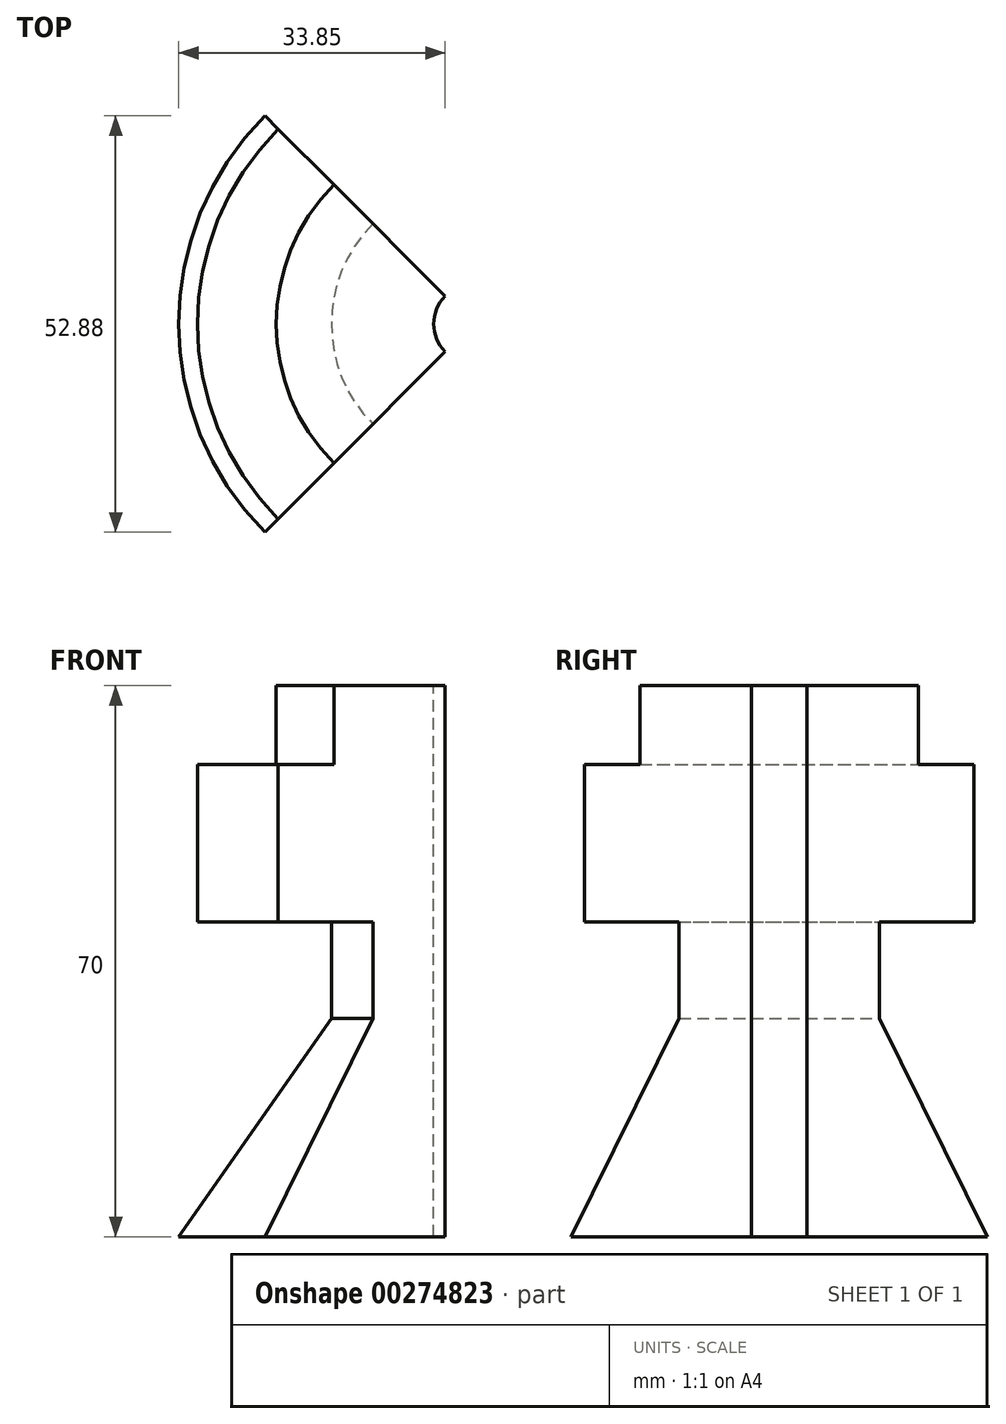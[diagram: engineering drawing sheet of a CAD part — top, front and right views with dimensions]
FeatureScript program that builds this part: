
annotation { "Feature Type Name" : "Feature", "Feature Type Description" : "" }
export const myFeature = defineFeature(function(context is Context, id is Id, definition is map)
    precondition{}
    {
        {
            var Q0;
            Q0=qCreatedBy(makeId("Front.planeOp"),FACE);
            var sketch = newSketch(context, id + "F0", { "sketchPlane" : qUnion([Q0])});
            skLineSegment(sketch, "E0", {"start": v(0, 0) * mm, "end": v(0, 40) * mm});
            skLineSegment(sketch, "E1", {"start": v(0, 40) * mm, "end": v(-25, 40) * mm});
            skLineSegment(sketch, "E2", {"start": v(-25, 40) * mm, "end": v(-25, 30) * mm});
            skLineSegment(sketch, "E3", {"start": v(-25, 30) * mm, "end": v(-35, 30) * mm});
            skLineSegment(sketch, "E4", {"start": v(-35, 30) * mm, "end": v(-35, 10) * mm});
            skLineSegment(sketch, "E5", {"start": v(-35, 10) * mm, "end": v(-18, 10) * mm});
            skLineSegment(sketch, "E6", {"start": v(-18, 10) * mm, "end": v(-18, -2.3) * mm});
            skLineSegment(sketch, "E7", {"start": v(-18, -2.3) * mm, "end": v(-37.4, -30) * mm});
            skLineSegment(sketch, "E8", {"start": v(-37.4, -30) * mm, "end": v(0, -30) * mm});
            skLineSegment(sketch, "E9", {"start": v(0, -30) * mm, "end": v(0, 0) * mm});
            skSolve(sketch);
        }
        {
            var Q0;
            Q0 = qSketchRegion(id + "F0", true);
            var Q1;
            Q1=sQuery(id+"F0.wireOp",EDGE,"E0");
            revolve(context, id + "F1", {"entities" : qUnion([Q0]), "axis" : qUnion([Q1]), "revolveType" : RevolveType.SYMMETRIC, "angle" : 90 * degree});
        }
        {
            var Q0;
            Q0=makeQuery(id+"F1.opRevolve","SWEPT_FACE",FACE,{"disambiguationData":[OSD([sQuery(id+"F0.wireOp",EDGE,"E1")])]});
            var sketch = newSketch(context, id + "F2", { "sketchPlane" : qUnion([Q0])});
            skCircle(sketch, "E10", {"center": v(0, 0) * mm, "radius": 5 * mm});
            skSolve(sketch);
        }
        {
            var Q0;
            Q0=makeQuery(id+"F2.imprint","IMPRINT",FACE,{"disambiguationData":[TD([[makeQuery(id+"F2.imprint","IMPRINT",EDGE,{"derivedFrom":sQuery(id+"F2.wireOp",EDGE,"E10")}),1.0]])]});
            extrude(context, id + "F3", {"entities" : qUnion([Q0]), "operationType" : NewBodyOperationType.REMOVE, "endBound" : BoundingType.THROUGH_ALL, "oppositeDirection" : true, "depth" : 25 * mm});
        }
    });
